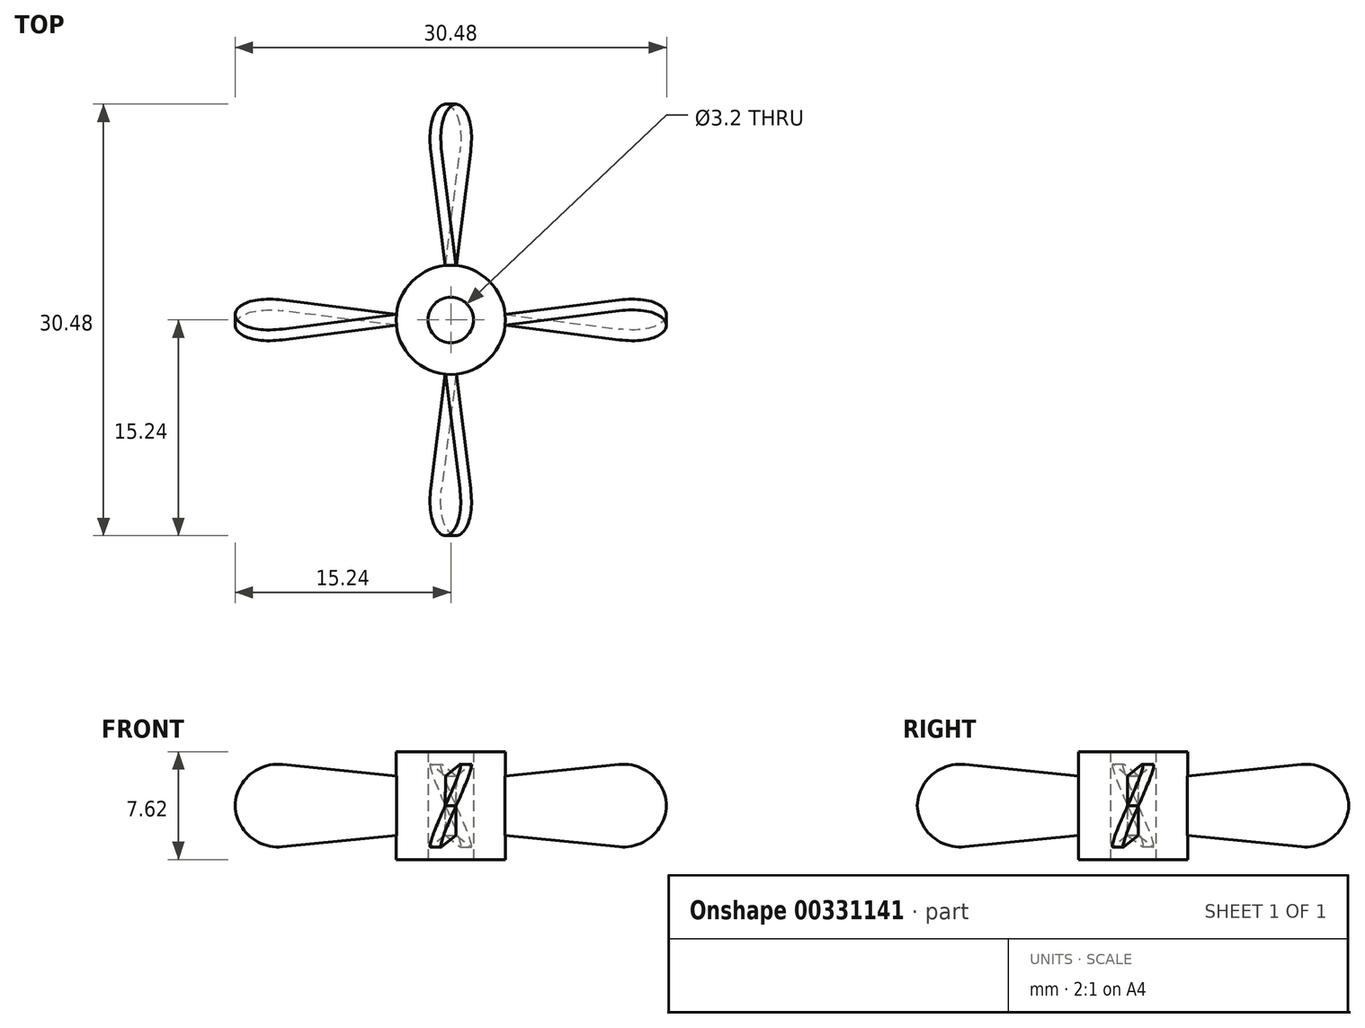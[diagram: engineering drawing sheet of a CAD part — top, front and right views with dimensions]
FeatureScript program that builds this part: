
annotation { "Feature Type Name" : "Feature", "Feature Type Description" : "" }
export const myFeature = defineFeature(function(context is Context, id is Id, definition is map)
    precondition{}
    {
        {
            var Q0;
            Q0=qCreatedBy(makeId("Top.planeOp"),FACE);
            var sketch = newSketch(context, id + "F0", { "sketchPlane" : qUnion([Q0])});
            skCircle(sketch, "E0", {"center": v(0, 0) * mm, "radius": 3.86 * mm});
            skSolve(sketch);
        }
        {
            var Q0;
            Q0=qCreatedBy(makeId("Top.planeOp"),FACE);
            var sketch = newSketch(context, id + "F1", { "sketchPlane" : qUnion([Q0])});
            skLineSegment(sketch, "E1.bottom", {"start": v(1.61, -1.61) * mm, "end": v(-1.61, -1.61) * mm});
            skLineSegment(sketch, "E1.top", {"start": v(1.61, 1.61) * mm, "end": v(-1.61, 1.61) * mm});
            skLineSegment(sketch, "E1.left", {"start": v(1.61, -1.61) * mm, "end": v(1.61, 1.61) * mm});
            skLineSegment(sketch, "E1.right", {"start": v(-1.61, -1.61) * mm, "end": v(-1.61, 1.61) * mm});
            skPoint(sketch, "E1.middle", {"position": v(0, 0) * mm});
            skSolve(sketch);
        }
        {
            var Q0;
            Q0 = qSketchRegion(id + "F0", true);
            extrude(context, id + "F2", {"entities" : qUnion([Q0]), "depth" : 3.8 * mm, "hasSecondDirection" : true, "secondDirectionOppositeDirection" : true, "secondDirectionDepth" : 3.8 * mm});
        }
        {
            var Q0;
            Q0=makeQuery(id+"F2.opExtrude","CAP_FACE",FACE,{"disambiguationData":[OSD([sQuery(id+"F0.wireOp",EDGE,"E0")])],"isStart":true});
            var sketch = newSketch(context, id + "F3", { "sketchPlane" : qUnion([Q0])});
            skPoint(sketch, "E2", {"position": v(0, 0) * mm});
            skSolve(sketch);
        }
        {
            var Q0;
            Q0=sQuery(id+"F3.wireOp",VERTEX,"E2");
            var Q1;
            Q1=makeQuery(id+"F2.opExtrude","SWEPT_BODY",BODY,{"disambiguationData":[OSD([sQuery(id+"F0.wireOp",EDGE,"E0")])]});
            hole(context, id + "F4", {"style" : HoleStyle.SIMPLE, "endStyle" : HoleEndStyle.THROUGH, "holeDiameter" : 3.2 * mm, "isTappedThrough" : true, "tappedDepth" : 12.7 * mm, "tapClearance" : 3, "locations" : qUnion([Q0]), "scope" : qUnion([Q1])});
        }
        {
            var Q0;
            Q0=qCreatedBy(makeId("Right.planeOp"),FACE);
            cPlane(context, id + "F5", {"entities" : qUnion([Q0]), "cplaneType" : CPlaneType.OFFSET, "offset" : 3.8 * mm, "width" : 152.4 * mm, "height" : 152.4 * mm});
        }
        {
            var Q0;
            Q0=qCreatedBy(id+"F5.planeOp",FACE);
            var sketch = newSketch(context, id + "F6", { "sketchPlane" : qUnion([Q0])});
            skLineSegment(sketch, "E3.bottom", {"start": v(0.38, -2.1) * mm, "end": v(-0.38, -2.1) * mm});
            skLineSegment(sketch, "E3.top", {"start": v(0.38, 2.1) * mm, "end": v(-0.38, 2.1) * mm});
            skLineSegment(sketch, "E3.left", {"start": v(0.38, -2.1) * mm, "end": v(0.38, 2.1) * mm});
            skLineSegment(sketch, "E3.right", {"start": v(-0.38, -2.1) * mm, "end": v(-0.38, 2.1) * mm});
            skPoint(sketch, "E3.middle", {"position": v(0, 0) * mm});
            skSolve(sketch);
        }
        {
            var Q0;
            Q0=qCreatedBy(id+"F5.planeOp",FACE);
            cPlane(context, id + "F7", {"entities" : qUnion([Q0]), "cplaneType" : CPlaneType.OFFSET, "offset" : 11.43 * mm, "width" : 152.4 * mm, "height" : 152.4 * mm});
        }
        {
            var Q0;
            Q0=qCreatedBy(makeId("Front.planeOp"),FACE);
            cPlane(context, id + "F8", {"entities" : qUnion([Q0]), "cplaneType" : CPlaneType.OFFSET, "offset" : 3.8 * mm, "oppositeDirection" : true, "width" : 152.4 * mm, "height" : 152.4 * mm});
        }
        {
            var Q0;
            Q0=qCreatedBy(id+"F8.planeOp",FACE);
            cPlane(context, id + "F9", {"entities" : qUnion([Q0]), "cplaneType" : CPlaneType.OFFSET, "offset" : 11.43 * mm, "oppositeDirection" : true, "width" : 152.4 * mm, "height" : 152.4 * mm});
        }
        {
            var Q0;
            Q0=qCreatedBy(id+"F8.planeOp",FACE);
            var sketch = newSketch(context, id + "F10", { "sketchPlane" : qUnion([Q0])});
            skLineSegment(sketch, "E4.bottom", {"start": v(0.38, -2.1) * mm, "end": v(-0.38, -2.1) * mm});
            skLineSegment(sketch, "E4.top", {"start": v(0.38, 2.1) * mm, "end": v(-0.38, 2.1) * mm});
            skLineSegment(sketch, "E4.left", {"start": v(0.38, -2.1) * mm, "end": v(0.38, 2.1) * mm});
            skLineSegment(sketch, "E4.right", {"start": v(-0.38, -2.1) * mm, "end": v(-0.38, 2.1) * mm});
            skPoint(sketch, "E4.middle", {"position": v(0, 0) * mm});
            skSolve(sketch);
        }
        {
            var Q0;
            Q0=qCreatedBy(id+"F9.planeOp",FACE);
            var sketch = newSketch(context, id + "F11", { "sketchPlane" : qUnion([Q0])});
            skLineSegment(sketch, "E5.bottom", {"start": v(1.07, -3.25) * mm, "end": v(1.83, -3.25) * mm});
            skLineSegment(sketch, "E5.top", {"start": v(-1.83, 3.25) * mm, "end": v(-1.07, 3.25) * mm});
            skLineSegment(sketch, "E5.left", {"start": v(1.07, -3.25) * mm, "end": v(-1.83, 3.25) * mm});
            skLineSegment(sketch, "E5.right", {"start": v(1.83, -3.25) * mm, "end": v(-1.07, 3.25) * mm});
            skPoint(sketch, "E5.middle", {"position": v(0, 0) * mm});
            skSolve(sketch);
        }
        {
            var Q0;
            Q0=qCreatedBy(makeId("Right.planeOp"),FACE);
            cPlane(context, id + "F12", {"entities" : qUnion([Q0]), "cplaneType" : CPlaneType.OFFSET, "offset" : 3.8 * mm, "oppositeDirection" : true, "width" : 152.4 * mm, "height" : 152.4 * mm});
        }
        {
            var Q0;
            Q0=qCreatedBy(id+"F12.planeOp",FACE);
            cPlane(context, id + "F13", {"entities" : qUnion([Q0]), "cplaneType" : CPlaneType.OFFSET, "offset" : 11.43 * mm, "oppositeDirection" : true, "width" : 152.4 * mm, "height" : 152.4 * mm});
        }
        {
            var Q0;
            Q0=qCreatedBy(id+"F12.planeOp",FACE);
            var sketch = newSketch(context, id + "F14", { "sketchPlane" : qUnion([Q0])});
            skLineSegment(sketch, "E6.bottom", {"start": v(-0.38, -2.1) * mm, "end": v(0.38, -2.1) * mm});
            skLineSegment(sketch, "E6.top", {"start": v(-0.38, 2.1) * mm, "end": v(0.38, 2.1) * mm});
            skLineSegment(sketch, "E6.left", {"start": v(-0.38, -2.1) * mm, "end": v(-0.38, 2.1) * mm});
            skLineSegment(sketch, "E6.right", {"start": v(0.38, -2.1) * mm, "end": v(0.38, 2.1) * mm});
            skPoint(sketch, "E6.middle", {"position": v(0, 0) * mm});
            skSolve(sketch);
        }
        {
            var Q0;
            Q0=qCreatedBy(makeId("Front.planeOp"),FACE);
            cPlane(context, id + "F15", {"entities" : qUnion([Q0]), "cplaneType" : CPlaneType.OFFSET, "offset" : 3.8 * mm, "width" : 152.4 * mm, "height" : 152.4 * mm});
        }
        {
            var Q0;
            Q0=qCreatedBy(id+"F15.planeOp",FACE);
            cPlane(context, id + "F16", {"entities" : qUnion([Q0]), "cplaneType" : CPlaneType.OFFSET, "offset" : 11.43 * mm, "width" : 152.4 * mm, "height" : 152.4 * mm});
        }
        {
            var Q0;
            Q0=qCreatedBy(id+"F15.planeOp",FACE);
            var sketch = newSketch(context, id + "F17", { "sketchPlane" : qUnion([Q0])});
            skLineSegment(sketch, "E7.bottom", {"start": v(0.38, -2.1) * mm, "end": v(-0.38, -2.1) * mm});
            skLineSegment(sketch, "E7.top", {"start": v(0.38, 2.1) * mm, "end": v(-0.38, 2.1) * mm});
            skLineSegment(sketch, "E7.left", {"start": v(0.38, -2.1) * mm, "end": v(0.38, 2.1) * mm});
            skLineSegment(sketch, "E7.right", {"start": v(-0.38, -2.1) * mm, "end": v(-0.38, 2.1) * mm});
            skPoint(sketch, "E7.middle", {"position": v(0, 0) * mm});
            skSolve(sketch);
        }
        {
            var Q0;
            Q0=qCreatedBy(id+"F16.planeOp",FACE);
            var sketch = newSketch(context, id + "F18", { "sketchPlane" : qUnion([Q0])});
            skLineSegment(sketch, "E8.bottom", {"start": v(-1.07, -3.25) * mm, "end": v(-1.83, -3.25) * mm});
            skLineSegment(sketch, "E8.top", {"start": v(1.83, 3.25) * mm, "end": v(1.07, 3.25) * mm});
            skLineSegment(sketch, "E8.left", {"start": v(-1.07, -3.25) * mm, "end": v(1.83, 3.25) * mm});
            skLineSegment(sketch, "E8.right", {"start": v(-1.83, -3.25) * mm, "end": v(1.07, 3.25) * mm});
            skPoint(sketch, "E8.middle", {"position": v(0, 0) * mm});
            skSolve(sketch);
        }
        {
            var Q0;
            Q0=qCreatedBy(id+"F13.planeOp",FACE);
            var sketch = newSketch(context, id + "F19", { "sketchPlane" : qUnion([Q0])});
            skLineSegment(sketch, "E9.bottom", {"start": v(1.83, -3.25) * mm, "end": v(1.07, -3.25) * mm});
            skLineSegment(sketch, "E9.top", {"start": v(-1.07, 3.25) * mm, "end": v(-1.83, 3.25) * mm});
            skLineSegment(sketch, "E9.left", {"start": v(1.83, -3.25) * mm, "end": v(-1.07, 3.25) * mm});
            skLineSegment(sketch, "E9.right", {"start": v(1.07, -3.25) * mm, "end": v(-1.83, 3.25) * mm});
            skPoint(sketch, "E9.middle", {"position": v(0, 0) * mm});
            skSolve(sketch);
        }
        {
            var Q0;
            Q0=qCreatedBy(id+"F7.planeOp",FACE);
            var sketch = newSketch(context, id + "F20", { "sketchPlane" : qUnion([Q0])});
            skLineSegment(sketch, "E10.bottom", {"start": v(-1.07, -3.25) * mm, "end": v(-1.83, -3.25) * mm});
            skLineSegment(sketch, "E10.top", {"start": v(1.83, 3.25) * mm, "end": v(1.07, 3.25) * mm});
            skLineSegment(sketch, "E10.left", {"start": v(-1.07, -3.25) * mm, "end": v(1.83, 3.25) * mm});
            skLineSegment(sketch, "E10.right", {"start": v(-1.83, -3.25) * mm, "end": v(1.07, 3.25) * mm});
            skPoint(sketch, "E10.middle", {"position": v(0, 0) * mm});
            skSolve(sketch);
        }
        {
            var Q1;
            Q1 = qSketchRegion(id + "F6", true);
            var Q2;
            Q2=makeQuery(id+"F20.imprint","IMPRINT",FACE,{"disambiguationData":[TD([[makeQuery(id+"F20.imprint","IMPRINT",EDGE,{"derivedFrom":sQuery(id+"F20.wireOp",EDGE,"E10.bottom")}),-1.0]])]});
            loft(context, id + "F21", {"operationType" : NewBodyOperationType.ADD, "sheetProfilesArray" : [{ "sheetProfileEntities" : qUnion([Q1]) }, { "sheetProfileEntities" : qUnion([Q2]) }]});
        }
        {
            var Q1;
            Q1 = qSketchRegion(id + "F10", true);
            var Q2;
            Q2=makeQuery(id+"F11.imprint","IMPRINT",FACE,{"disambiguationData":[TD([[makeQuery(id+"F11.imprint","IMPRINT",EDGE,{"derivedFrom":sQuery(id+"F11.wireOp",EDGE,"E5.bottom")}),1.0]])]});
            loft(context, id + "F22", {"operationType" : NewBodyOperationType.ADD, "sheetProfilesArray" : [{ "sheetProfileEntities" : qUnion([Q1]) }, { "sheetProfileEntities" : qUnion([Q2]) }]});
        }
        {
            var Q1;
            Q1 = qSketchRegion(id + "F14", true);
            var Q2;
            Q2=makeQuery(id+"F19.imprint","IMPRINT",FACE,{"disambiguationData":[TD([[makeQuery(id+"F19.imprint","IMPRINT",EDGE,{"derivedFrom":sQuery(id+"F19.wireOp",EDGE,"E9.bottom")}),-1.0]])]});
            loft(context, id + "F23", {"operationType" : NewBodyOperationType.ADD, "sheetProfilesArray" : [{ "sheetProfileEntities" : qUnion([Q1]) }, { "sheetProfileEntities" : qUnion([Q2]) }]});
        }
        {
            var Q1;
            Q1 = qSketchRegion(id + "F17", true);
            var Q2;
            Q2=makeQuery(id+"F18.imprint","IMPRINT",FACE,{"disambiguationData":[TD([[makeQuery(id+"F18.imprint","IMPRINT",EDGE,{"derivedFrom":sQuery(id+"F18.wireOp",EDGE,"E8.bottom")}),-1.0]])]});
            loft(context, id + "F24", {"operationType" : NewBodyOperationType.ADD, "sheetProfilesArray" : [{ "sheetProfileEntities" : qUnion([Q1]) }, { "sheetProfileEntities" : qUnion([Q2]) }]});
        }
        {
            var Q0;
            Q0=makeQuery(id+"F23.opLoft","MID_CAP_EDGE",EDGE,{"disambiguationData":[OSD([sQuery(id+"F19.wireOp",EDGE,"E9.top"),sQuery(id+"F19.wireOp",EDGE,"E9.left"),sQuery(id+"F19.wireOp",EDGE,"E9.right")])],"capPos":1.0});
            var Q1;
            Q1=makeQuery(id+"F23.opLoft","MID_CAP_EDGE",EDGE,{"disambiguationData":[OSD([sQuery(id+"F19.wireOp",EDGE,"E9.bottom"),sQuery(id+"F19.wireOp",EDGE,"E9.left"),sQuery(id+"F19.wireOp",EDGE,"E9.right")])],"capPos":1.0});
            var Q2;
            Q2=makeQuery(id+"F22.opLoft","MID_CAP_EDGE",EDGE,{"disambiguationData":[OSD([sQuery(id+"F11.wireOp",EDGE,"E5.bottom"),sQuery(id+"F11.wireOp",EDGE,"E5.left"),sQuery(id+"F11.wireOp",EDGE,"E5.right")])],"capPos":1.0});
            var Q3;
            Q3=makeQuery(id+"F22.opLoft","MID_CAP_EDGE",EDGE,{"disambiguationData":[OSD([sQuery(id+"F11.wireOp",EDGE,"E5.top"),sQuery(id+"F11.wireOp",EDGE,"E5.left"),sQuery(id+"F11.wireOp",EDGE,"E5.right")])],"capPos":1.0});
            var Q4;
            Q4=makeQuery(id+"F24.opLoft","MID_CAP_EDGE",EDGE,{"disambiguationData":[OSD([sQuery(id+"F18.wireOp",EDGE,"E8.top"),sQuery(id+"F18.wireOp",EDGE,"E8.left"),sQuery(id+"F18.wireOp",EDGE,"E8.right")])],"capPos":1.0});
            var Q5;
            Q5=makeQuery(id+"F24.opLoft","MID_CAP_EDGE",EDGE,{"disambiguationData":[OSD([sQuery(id+"F18.wireOp",EDGE,"E8.bottom"),sQuery(id+"F18.wireOp",EDGE,"E8.left"),sQuery(id+"F18.wireOp",EDGE,"E8.right")])],"capPos":1.0});
            var Q6;
            Q6=makeQuery(id+"F21.opLoft","MID_CAP_EDGE",EDGE,{"disambiguationData":[OSD([sQuery(id+"F20.wireOp",EDGE,"E10.top"),sQuery(id+"F20.wireOp",EDGE,"E10.left"),sQuery(id+"F20.wireOp",EDGE,"E10.right")])],"capPos":1.0});
            var Q7;
            Q7=makeQuery(id+"F21.opLoft","MID_CAP_EDGE",EDGE,{"disambiguationData":[OSD([sQuery(id+"F20.wireOp",EDGE,"E10.bottom"),sQuery(id+"F20.wireOp",EDGE,"E10.left"),sQuery(id+"F20.wireOp",EDGE,"E10.right")])],"capPos":1.0});
            fillet(context, id + "F25", {"entities" : qUnion([Q0, Q1, Q2, Q3, Q4, Q5, Q6, Q7]), "radius" : 3.05 * mm, "tangentPropagation" : true, "allowEdgeOverflow" : false});
        }
    });
